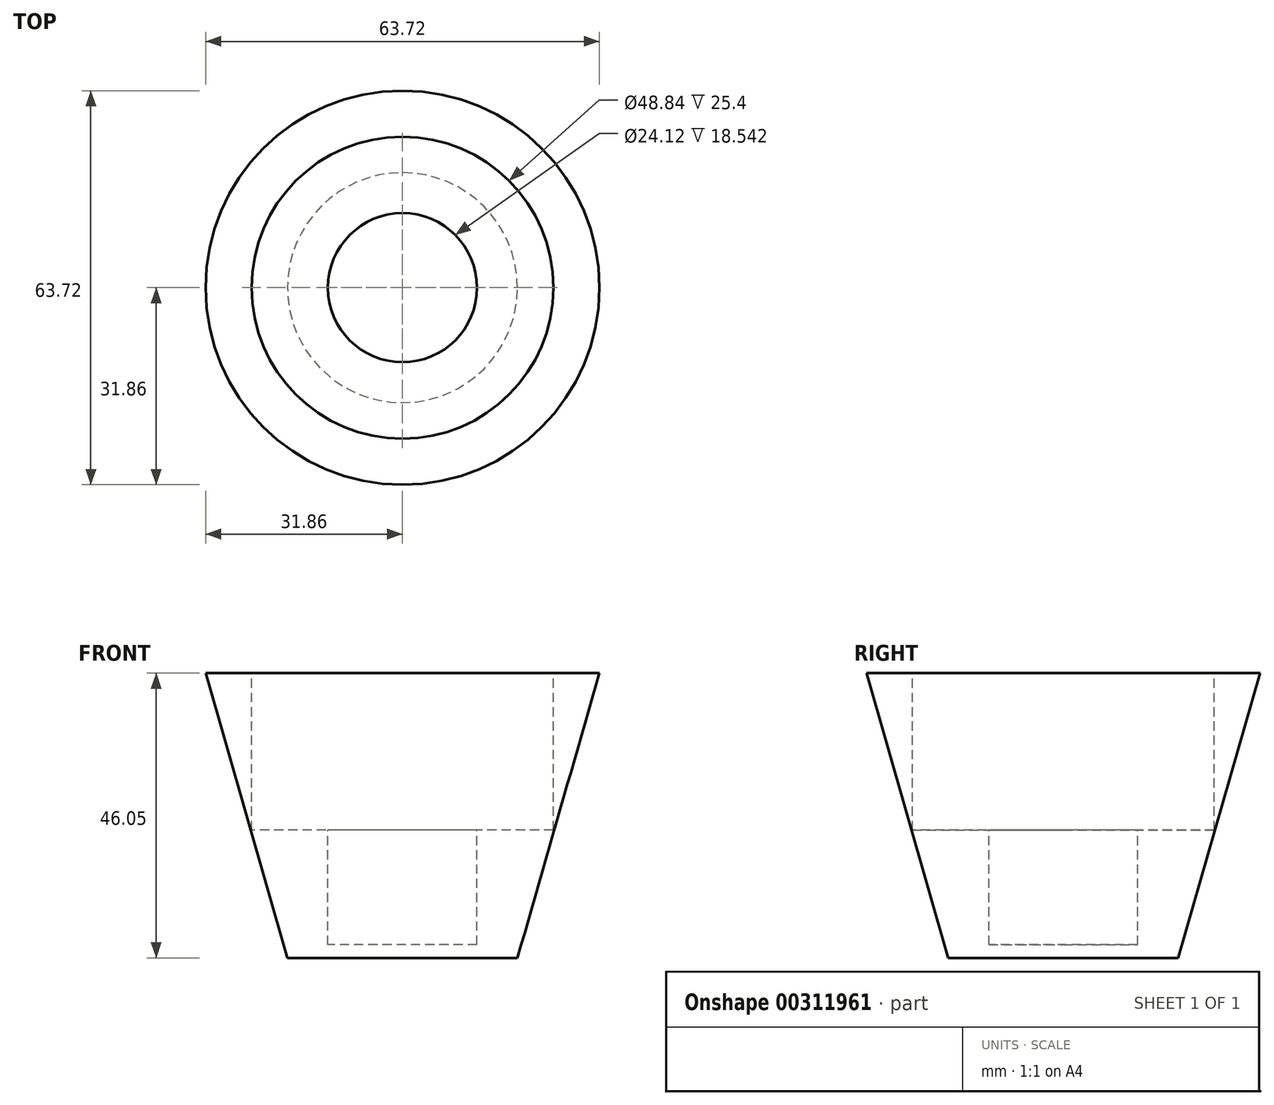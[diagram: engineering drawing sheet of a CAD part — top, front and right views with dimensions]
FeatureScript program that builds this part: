
annotation { "Feature Type Name" : "Feature", "Feature Type Description" : "" }
export const myFeature = defineFeature(function(context is Context, id is Id, definition is map)
    precondition{}
    {
        {
            var Q0;
            Q0=qCreatedBy(makeId("Front.planeOp"),FACE);
            var sketch = newSketch(context, id + "F0", { "sketchPlane" : qUnion([Q0])});
            skLineSegment(sketch, "E0", {"start": v(0, 20) * mm, "end": v(0, -26.05) * mm});
            skLineSegment(sketch, "E1", {"start": v(0, -26.05) * mm, "end": v(-18.6, -26.05) * mm});
            skLineSegment(sketch, "E2", {"start": v(-18.6, -26.05) * mm, "end": v(-31.86, 20) * mm});
            skLineSegment(sketch, "E3", {"start": v(-31.86, 20) * mm, "end": v(0, 20) * mm});
            skSolve(sketch);
        }
        {
            var Q0;
            Q0 = qSketchRegion(id + "F0", true);
            var Q1;
            Q1=sQuery(id+"F0.wireOp",EDGE,"E0");
            revolve(context, id + "F1", {"entities" : qUnion([Q0]), "axis" : qUnion([Q1]), "revolveType" : RevolveType.FULL});
        }
        {
            var Q0;
            Q0=makeQuery(id+"F1.opRevolve","SWEPT_FACE",FACE,{"disambiguationData":[OSD([sQuery(id+"F0.wireOp",EDGE,"E3")])]});
            var sketch = newSketch(context, id + "F2", { "sketchPlane" : qUnion([Q0])});
            skCircle(sketch, "E4", {"center": v(0, 0) * mm, "radius": 24.42 * mm});
            skSolve(sketch);
        }
        {
            var Q0;
            Q0 = qSketchRegion(id + "F2", true);
            extrude(context, id + "F3", {"entities" : qUnion([Q0]), "operationType" : NewBodyOperationType.REMOVE, "oppositeDirection" : true, "depth" : 25.4 * mm});
        }
        {
            var Q0;
            Q0=makeQuery(id+"F3.boolean.opBoolean","COPY",FACE,{"derivedFrom":makeQuery(id+"F3.opExtrude","CAP_FACE",FACE,{"disambiguationData":[OSD([sQuery(id+"F2.wireOp",EDGE,"E4")])],"isStart":false})});
            var sketch = newSketch(context, id + "F4", { "sketchPlane" : qUnion([Q0])});
            skCircle(sketch, "E5", {"center": v(0, 0) * mm, "radius": 12.06 * mm});
            skSolve(sketch);
        }
        {
            var Q0;
            Q0 = qSketchRegion(id + "F4", true);
            extrude(context, id + "F5", {"entities" : qUnion([Q0]), "operationType" : NewBodyOperationType.REMOVE, "oppositeDirection" : true, "depth" : 18.54 * mm});
        }
    });
